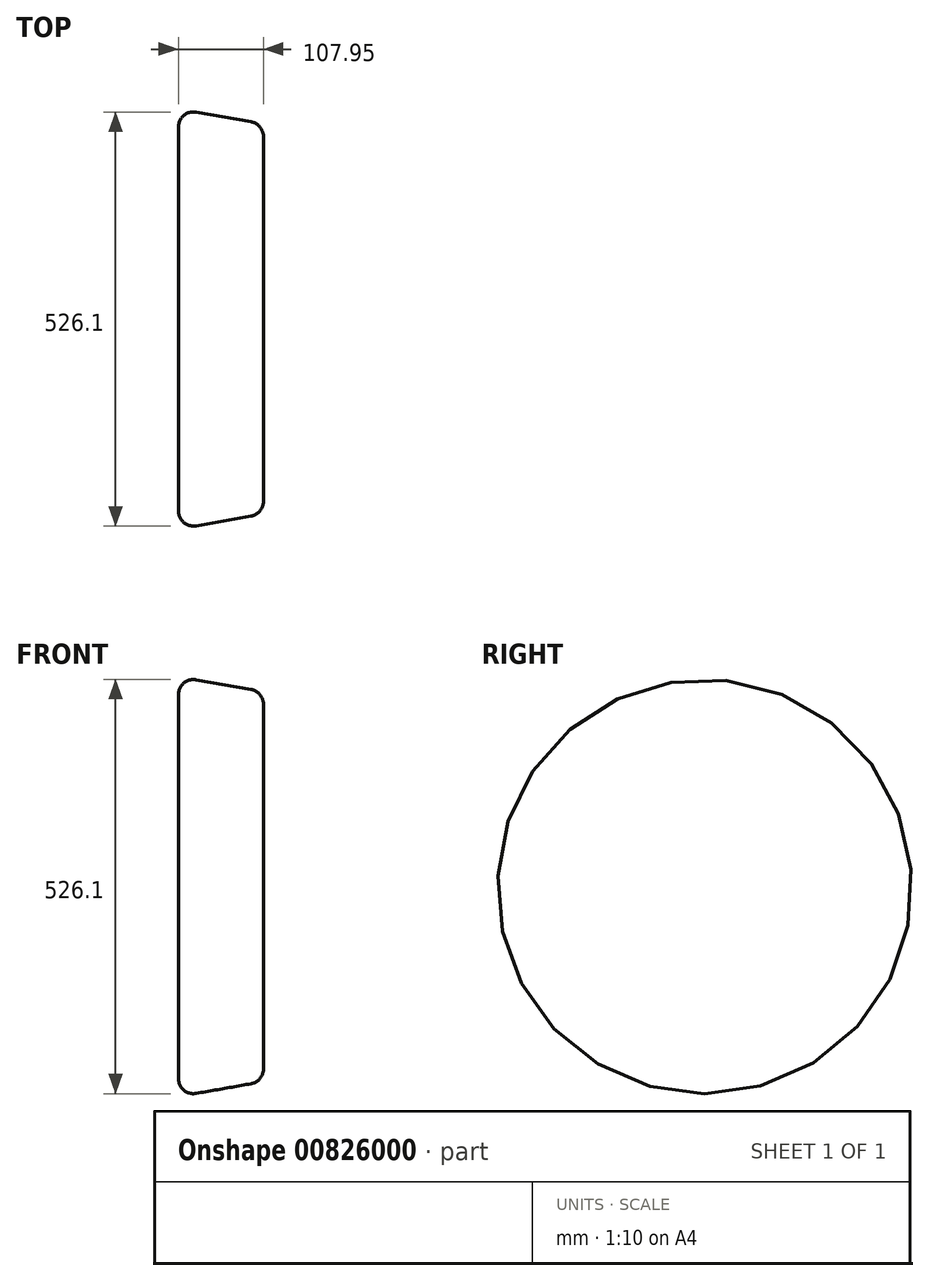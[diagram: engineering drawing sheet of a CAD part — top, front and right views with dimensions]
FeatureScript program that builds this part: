
annotation { "Feature Type Name" : "Feature", "Feature Type Description" : "" }
export const myFeature = defineFeature(function(context is Context, id is Id, definition is map)
    precondition{}
    {
        {
            var Q0;
            Q0=qCreatedBy(makeId("Top.planeOp"),FACE);
            var sketch = newSketch(context, id + "F0", { "sketchPlane" : qUnion([Q0])});
            skCircle(sketch, "E0", {"center": v(0, 0) * mm, "radius": 56.52 * mm});
            skSolve(sketch);
        }
        {
            var Q0;
            Q0=qCreatedBy(makeId("Right.planeOp"),FACE);
            var sketch = newSketch(context, id + "F1", { "sketchPlane" : qUnion([Q0])});
            skCircle(sketch, "E1", {"center": v(0, 0) * mm, "radius": 266.7 * mm});
            skSolve(sketch);
        }
        {
            var Q0;
            Q0=makeQuery(id+"F1.imprint","IMPRINT",FACE,{"disambiguationData":[TD([[makeQuery(id+"F1.imprint","IMPRINT",EDGE,{"derivedFrom":sQuery(id+"F1.wireOp",EDGE,"E1")}),1.0]])]});
            extrude(context, id + "F2", {"entities" : qUnion([Q0]), "depth" : 107.95 * mm, "offsetDistance" : 25.4 * mm, "hasDraft" : true, "draftAngle" : 10 * degree, "draftPullDirection" : true});
        }
        {
            var Q0;
            Q0=makeQuery(id+"F2.opExtrude","CAP_EDGE",EDGE,{"disambiguationData":[OSD([sQuery(id+"F1.wireOp",EDGE,"E1")])],"isStart":false});
            var Q1;
            Q1=makeQuery(id+"F2.opExtrude","CAP_EDGE",EDGE,{"disambiguationData":[OSD([sQuery(id+"F1.wireOp",EDGE,"E1")])],"isStart":true});
            fillet(context, id + "F3", {"entities" : qUnion([Q0, Q1]), "radius" : 19.05 * mm, "tangentPropagation" : true, "allowEdgeOverflow" : false});
        }
    });
